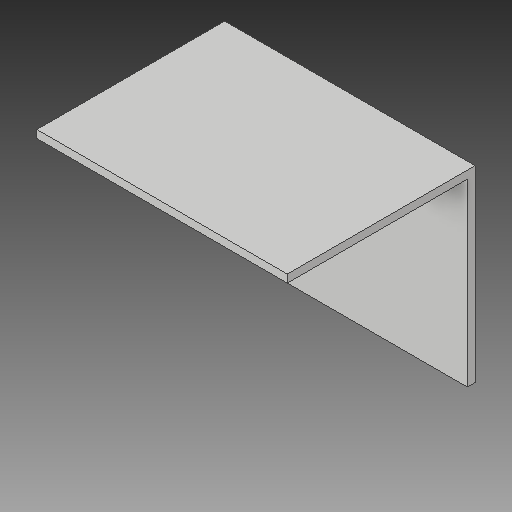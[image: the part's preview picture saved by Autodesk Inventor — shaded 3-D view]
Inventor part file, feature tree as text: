
AUTODESK INVENTOR PART (.ipt)
format: ipt  version: 2017 (Build 210142000, 142)  size: 82,432 bytes
history: native  units: in
note: dims shown in document units (in); Inventor stores cm internally (conversion verified against a paired STEP export)
features: other x3, sketch x1
ambient origin geometry x8: Origin, YZ Plane, XZ Plane, XY Plane, X Axis, Y Axis, Z Axis, Center Point
bodies: Solid1 (feature_tree)
feature tree (4):
  other  "corner piece 2x1.5.ipt"
  other  "Solid1::corner piece 2x1.5.ipt"
  other  "TaggingFeature1"
  sketch  "Sketch1"  dims[d0=0.3937in]
